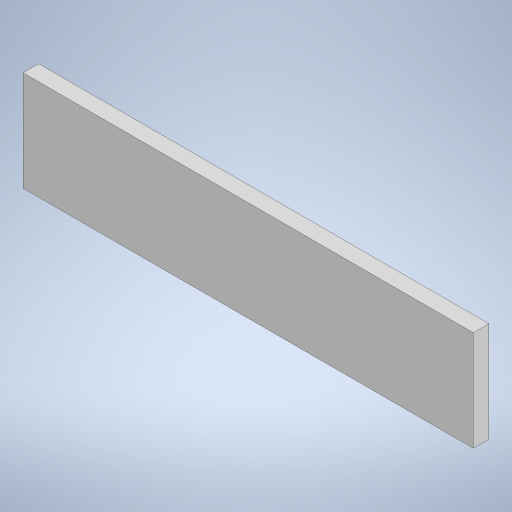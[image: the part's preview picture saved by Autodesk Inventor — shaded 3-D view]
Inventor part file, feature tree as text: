
AUTODESK INVENTOR PART (.ipt)
format: ipt  version: 2024 (Build 280153000, 153)  size: 204,288 bytes
history: native  units: mm
features: extrude x1, sketch x1
ambient origin geometry x8: Origin, YZ Plane, XZ Plane, XY Plane, X Axis, Y Axis, Z Axis, Center Point
bodies: Solid1 (feature_tree)
feature tree (2):
  extrude  "Extrusion1"  Depth=3.125mm
  sketch  "Sketch1"  dims[d0=90.0mm d1=3.125mm d2=20.0mm d3=0.0mm]
